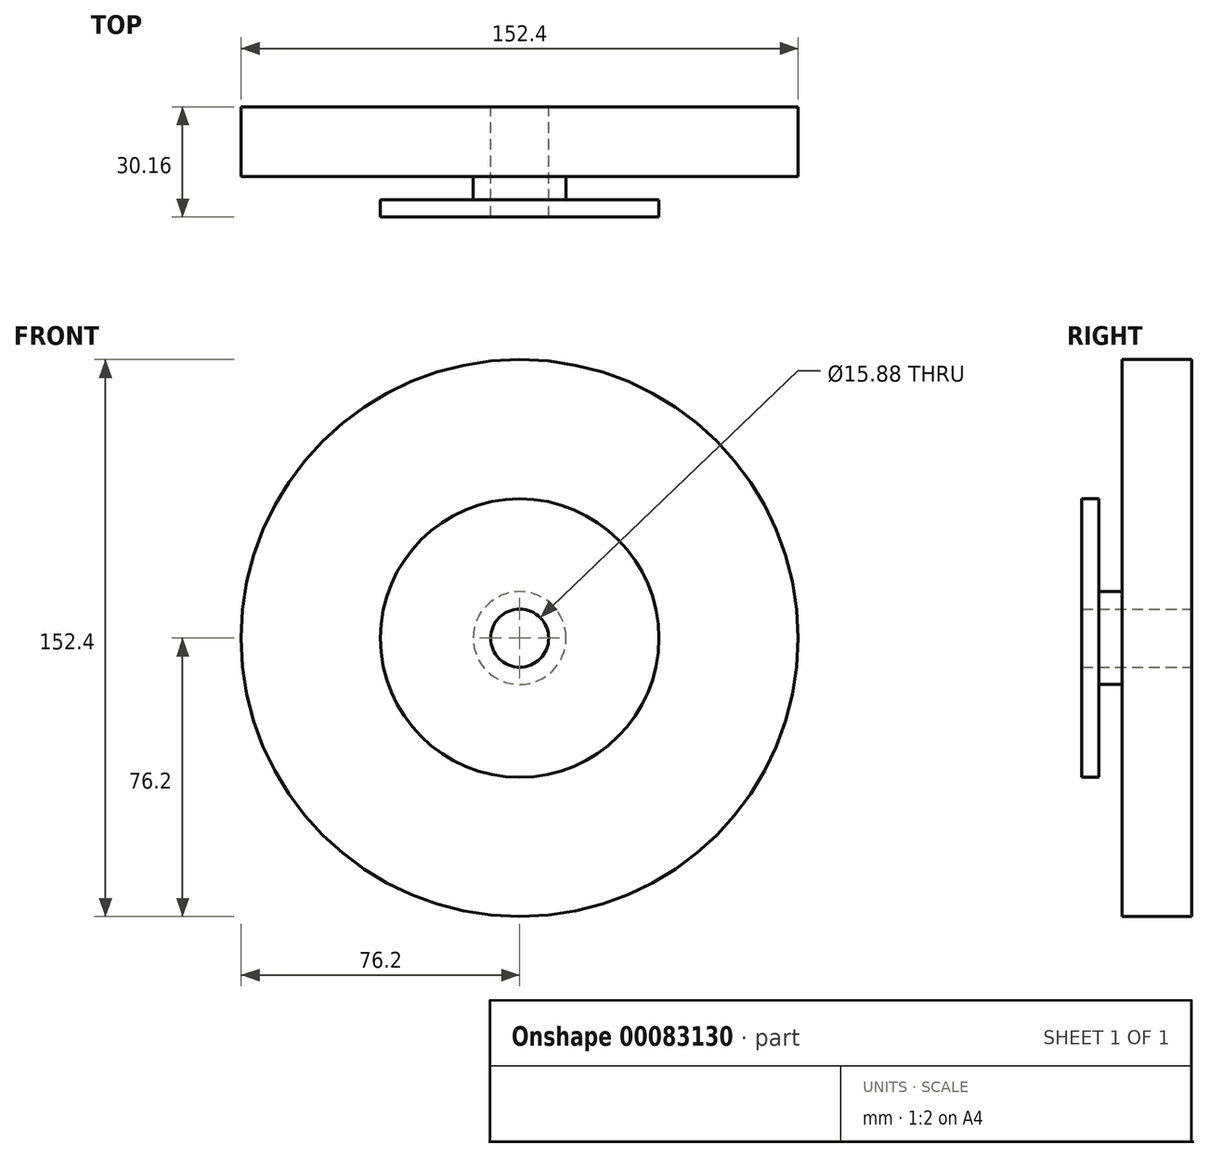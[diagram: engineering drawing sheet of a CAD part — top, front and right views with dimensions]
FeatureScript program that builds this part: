
annotation { "Feature Type Name" : "Feature", "Feature Type Description" : "" }
export const myFeature = defineFeature(function(context is Context, id is Id, definition is map)
    precondition{}
    {
        {
            var Q0;
            Q0=qCreatedBy(makeId("Front.planeOp"),FACE);
            var sketch = newSketch(context, id + "F0", { "sketchPlane" : qUnion([Q0])});
            skCircle(sketch, "E0", {"center": v(0, 0) * mm, "radius": 76.2 * mm});
            skCircle(sketch, "E1", {"center": v(0, 0) * mm, "radius": 7.94 * mm});
            skSolve(sketch);
        }
        {
            var Q0;
            Q0=makeQuery(id+"F0.imprint","IMPRINT",FACE,{"disambiguationData":[TD([[makeQuery(id+"F0.imprint","IMPRINT",EDGE,{"derivedFrom":sQuery(id+"F0.wireOp",EDGE,"E0")}),1.0]])]});
            extrude(context, id + "F1", {"entities" : qUnion([Q0]), "depth" : 19.05 * mm});
        }
        {
            var Q0;
            Q0=makeQuery(id+"F1.opExtrude","CAP_FACE",FACE,{"disambiguationData":[OSD([sQuery(id+"F0.wireOp",EDGE,"E0"),sQuery(id+"F0.wireOp",EDGE,"E1")])],"isStart":false});
            var sketch = newSketch(context, id + "F2", { "sketchPlane" : qUnion([Q0])});
            skCircle(sketch, "E2", {"center": v(0, 0) * mm, "radius": 12.7 * mm});
            skSolve(sketch);
        }
        {
            var Q0;
            Q0=makeQuery(id+"F2.imprint","IMPRINT",FACE,{"disambiguationData":[TD([[makeQuery(id+"F2.imprint","IMPRINT",EDGE,{"derivedFrom":sQuery(id+"F2.wireOp",EDGE,"E2")}),1.0]])]});
            extrude(context, id + "F3", {"entities" : qUnion([Q0]), "operationType" : NewBodyOperationType.ADD, "depth" : 6.35 * mm});
        }
        {
            var Q0;
            Q0=makeQuery(id+"F3.opExtrude","CAP_FACE",FACE,{"disambiguationData":[OSD([sQuery(id+"F2.wireOp",EDGE,"E2")])],"isStart":false});
            var sketch = newSketch(context, id + "F4", { "sketchPlane" : qUnion([Q0])});
            skCircle(sketch, "E3", {"center": v(0, 0) * mm, "radius": 38.1 * mm});
            skSolve(sketch);
        }
        {
            var Q0;
            Q0=makeQuery(id+"F4.imprint","IMPRINT",FACE,{"disambiguationData":[TD([[makeQuery(id+"F4.imprint","IMPRINT",EDGE,{"derivedFrom":makeQuery(id+"F3.opExtrude","CAP_EDGE",EDGE,{"disambiguationData":[OSD([sQuery(id+"F2.wireOp",EDGE,"E2")])],"isStart":false})}),1.0]])]});
            var Q1;
            Q1=makeQuery(id+"F4.imprint","IMPRINT",FACE,{"disambiguationData":[TD([[makeQuery(id+"F4.imprint","IMPRINT",EDGE,{"derivedFrom":sQuery(id+"F4.wireOp",EDGE,"E3")}),1.0]])]});
            extrude(context, id + "F5", {"entities" : qUnion([Q0, Q1]), "operationType" : NewBodyOperationType.ADD, "depth" : 4.76 * mm});
        }
    });
